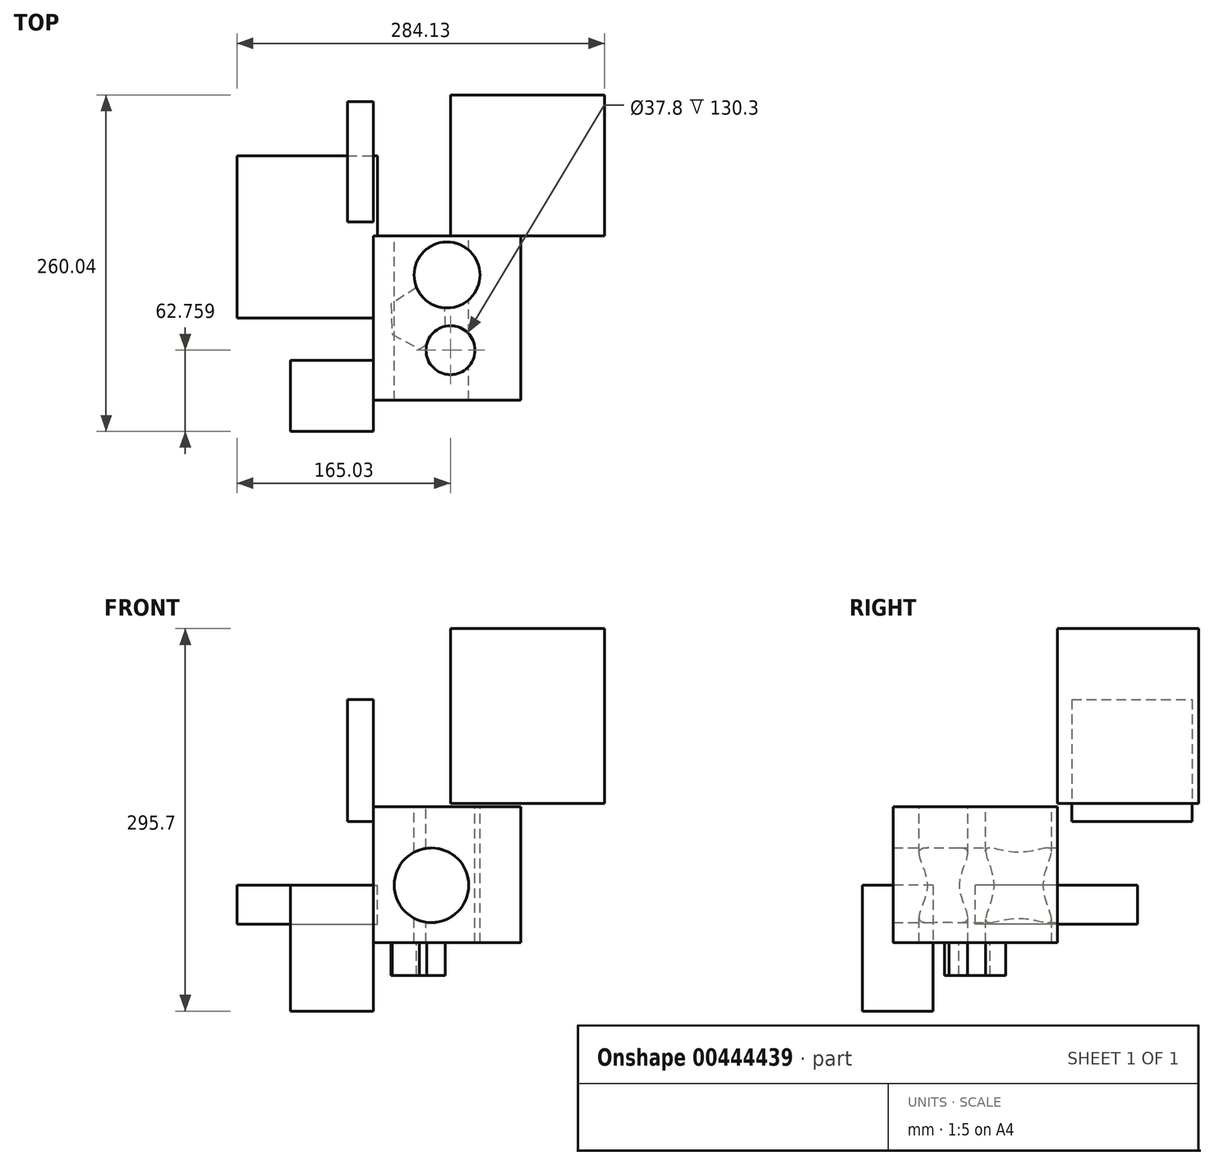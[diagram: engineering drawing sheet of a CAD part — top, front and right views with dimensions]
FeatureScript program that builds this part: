
annotation { "Feature Type Name" : "Feature", "Feature Type Description" : "" }
export const myFeature = defineFeature(function(context is Context, id is Id, definition is map)
    precondition{}
    {
        {
            var Q0;
            Q0=qCreatedBy(makeId("Front.planeOp"),FACE);
            var sketch = newSketch(context, id + "F0", { "sketchPlane" : qUnion([Q0])});
            skLineSegment(sketch, "E0.bottom", {"start": v(-59.68, 60.6) * mm, "end": v(54.4, 60.6) * mm});
            skLineSegment(sketch, "E0.top", {"start": v(-59.68, -44.3) * mm, "end": v(54.4, -44.3) * mm});
            skLineSegment(sketch, "E0.left", {"start": v(-59.68, 60.6) * mm, "end": v(-59.68, -44.3) * mm});
            skLineSegment(sketch, "E0.right", {"start": v(54.4, 60.6) * mm, "end": v(54.4, -44.3) * mm});
            skSolve(sketch);
        }
        {
            var Q0;
            Q0=makeQuery(id+"F0.imprint","IMPRINT",FACE,{"disambiguationData":[TD([[makeQuery(id+"F0.imprint","IMPRINT",EDGE,{"derivedFrom":sQuery(id+"F0.wireOp",EDGE,"E0.bottom")}),-1.0]])]});
            extrude(context, id + "F1", {"entities" : qUnion([Q0]), "endBound" : BoundingType.SYMMETRIC, "oppositeDirection" : true, "depth" : 127 * mm});
        }
        {
            var Q0;
            Q0=qCreatedBy(makeId("Front.planeOp"),FACE);
            var sketch = newSketch(context, id + "F2", { "sketchPlane" : qUnion([Q0])});
            skLineSegment(sketch, "E1", {"start": v(-104.47, 48.32) * mm, "end": v(17.34, -36.07) * mm});
            skLineSegment(sketch, "E2.0", {"start": v(-59.68, 60.6) * mm, "end": v(54.4, 60.6) * mm});
            skLineSegment(sketch, "E3.0.0", {"start": v(-59.68, 60.6) * mm, "end": v(-59.68, -44.3) * mm});
            skLineSegment(sketch, "E3.0.1", {"start": v(-59.68, -44.3) * mm, "end": v(54.4, -44.3) * mm});
            skLineSegment(sketch, "E3.0.2", {"start": v(54.4, -44.3) * mm, "end": v(54.4, 60.6) * mm});
            skLineSegment(sketch, "E3.0.3", {"start": v(54.4, 60.6) * mm, "end": v(-59.68, 60.6) * mm});
            skSolve(sketch);
        }
        {
            var Q0;
            Q0=makeQuery(id+"F1.opExtrude","CAP_FACE",FACE,{"disambiguationData":[OSD([sQuery(id+"F0.wireOp",EDGE,"E0.bottom"),sQuery(id+"F0.wireOp",EDGE,"E0.top"),sQuery(id+"F0.wireOp",EDGE,"E0.left"),sQuery(id+"F0.wireOp",EDGE,"E0.right")])],"isStart":false});
            var sketch = newSketch(context, id + "F3", { "sketchPlane" : qUnion([Q0])});
            skCircle(sketch, "E4", {"center": v(14.7, 0) * mm, "radius": 28.82 * mm});
            skSolve(sketch);
        }
        {
            var Q0;
            Q0=makeQuery(id+"F3.imprint","IMPRINT",FACE,{"disambiguationData":[TD([[makeQuery(id+"F3.imprint","IMPRINT",EDGE,{"derivedFrom":sQuery(id+"F3.wireOp",EDGE,"E4")}),1.0]])]});
            extrude(context, id + "F4", {"entities" : qUnion([Q0]), "operationType" : NewBodyOperationType.REMOVE, "oppositeDirection" : true, "depth" : 181.76 * mm});
        }
        {
            var Q0;
            Q0=makeQuery(id+"F1.opExtrude","SWEPT_FACE",FACE,{"disambiguationData":[OSD([sQuery(id+"F0.wireOp",EDGE,"E0.top")])]});
            var sketch = newSketch(context, id + "F5", { "sketchPlane" : qUnion([Q0])});
            skSolve(sketch);
        }
        {
            var Q0;
            {var subQ0=sQuery(id+"F0.wireOp",EDGE,"E0.top");Q0=makeQuery(id+"F5.imprint","IMPRINT",FACE,{"disambiguationData":[TD([[makeQuery(id+"F5.imprint","IMPRINT",EDGE,{"derivedFrom":makeQuery(id+"F1.opExtrude","CAP_EDGE",EDGE,{"disambiguationData":[OSD([subQ0])],"isStart":true})}),-1.0]])]});}
            var sketch = newSketch(context, id + "F6", { "sketchPlane" : qUnion([Q0])});
            skCircle(sketch, "E5.cCircle", {"center": v(-24.85, 0) * mm, "radius": 20.67 * mm, "construction": true});
            skLineSegment(sketch, "E5.0", {"start": v(-24.05, 23.85) * mm, "end": v(-3.8, 11.23) * mm});
            skLineSegment(sketch, "E5.1", {"start": v(-3.8, 11.23) * mm, "end": v(-4.6, -12.62) * mm});
            skLineSegment(sketch, "E5.2", {"start": v(-4.6, -12.62) * mm, "end": v(-25.65, -23.85) * mm});
            skLineSegment(sketch, "E5.3", {"start": v(-25.65, -23.85) * mm, "end": v(-45.9, -11.23) * mm});
            skLineSegment(sketch, "E5.4", {"start": v(-45.9, -11.23) * mm, "end": v(-45.1, 12.62) * mm});
            skLineSegment(sketch, "E5.5", {"start": v(-45.1, 12.62) * mm, "end": v(-24.05, 23.85) * mm});
            skPoint(sketch, "E5.0.midPoint", {"position": v(-13.93, 17.54) * mm});
            skSolve(sketch);
        }
        {
            var Q0;
            Q0=makeQuery(id+"F6.imprint","IMPRINT",FACE,{"disambiguationData":[TD([[makeQuery(id+"F6.imprint","IMPRINT",EDGE,{"derivedFrom":sQuery(id+"F6.wireOp",EDGE,"E5.0")}),-1.0]])]});
            extrude(context, id + "F7", {"entities" : qUnion([Q0]), "operationType" : NewBodyOperationType.ADD, "depth" : 25.4 * mm});
        }
        {
            var Q0;
            Q0 = qSketchRegion(id + "F2", true);
            var sketch = newSketch(context, id + "F8", { "sketchPlane" : qUnion([Q0])});
            skLineSegment(sketch, "E6.bottom", {"start": v(-165.03, -30.2) * mm, "end": v(-56.33, -30.2) * mm});
            skLineSegment(sketch, "E6.top", {"start": v(-165.03, 0) * mm, "end": v(-56.33, 0) * mm});
            skLineSegment(sketch, "E6.left", {"start": v(-165.03, -30.2) * mm, "end": v(-165.03, 0) * mm});
            skLineSegment(sketch, "E6.right", {"start": v(-56.33, -30.2) * mm, "end": v(-56.33, 0) * mm});
            skSolve(sketch);
        }
        {
            var Q0;
            Q0 = qSketchRegion(id + "F8", true);
            extrude(context, id + "F9", {"entities" : qUnion([Q0]), "operationType" : NewBodyOperationType.ADD, "oppositeDirection" : true, "depth" : 125.48 * mm});
        }
        {
            var Q0;
            Q0=makeQuery(id+"F1.opExtrude","SWEPT_FACE",FACE,{"disambiguationData":[OSD([sQuery(id+"F0.wireOp",EDGE,"E0.left")])]});
            var sketch = newSketch(context, id + "F10", { "sketchPlane" : qUnion([Q0])});
            skLineSegment(sketch, "E7", {"start": v(-116.28, 254.28) * mm, "end": v(-116.28, 223.5) * mm});
            skLineSegment(sketch, "E8", {"start": v(-116.28, 223.5) * mm, "end": v(0, 223.5) * mm});
            skLineSegment(sketch, "E9.bottom", {"start": v(-74.53, 143.6) * mm, "end": v(-167.43, 143.6) * mm});
            skLineSegment(sketch, "E9.top", {"start": v(-74.53, 49.3) * mm, "end": v(-167.43, 49.3) * mm});
            skLineSegment(sketch, "E9.left", {"start": v(-74.53, 143.6) * mm, "end": v(-74.53, 49.3) * mm});
            skLineSegment(sketch, "E9.right", {"start": v(-167.43, 143.6) * mm, "end": v(-167.43, 49.3) * mm});
            skSolve(sketch);
        }
        {
            var Q0;
            Q0 = qSketchRegion(id + "F10", true);
            extrude(context, id + "F11", {"entities" : qUnion([Q0]), "depth" : 20 * mm});
        }
        {
            var Q0;
            Q0=makeQuery(id+"F1.opExtrude","SWEPT_FACE",FACE,{"disambiguationData":[OSD([sQuery(id+"F0.wireOp",EDGE,"E0.bottom")])]});
            var sketch = newSketch(context, id + "F12", { "sketchPlane" : qUnion([Q0])});
            skCircle(sketch, "E10", {"center": v(0, -24.73) * mm, "radius": 18.9 * mm});
            skCircle(sketch, "E11", {"center": v(-2.64, 33.4) * mm, "radius": 25.5 * mm});
            skPoint(sketch, "E11.centerSnap0", {"position": v(-2.64, -63.5) * mm});
            skSolve(sketch);
        }
        {
            var Q0;
            Q0 = qSketchRegion(id + "F12", true);
            extrude(context, id + "F13", {"entities" : qUnion([Q0]), "operationType" : NewBodyOperationType.REMOVE, "oppositeDirection" : true, "depth" : 174.7 * mm});
        }
        {
            var Q0;
            Q0=makeQuery(id+"F1.opExtrude","SWEPT_FACE",FACE,{"disambiguationData":[OSD([sQuery(id+"F0.wireOp",EDGE,"E0.left")])]});
            var sketch = newSketch(context, id + "F14", { "sketchPlane" : qUnion([Q0])});
            skLineSegment(sketch, "E12.bottom", {"start": v(32.6, 0) * mm, "end": v(87.49, 0) * mm});
            skLineSegment(sketch, "E12.top", {"start": v(32.6, -97.27) * mm, "end": v(87.49, -97.27) * mm});
            skLineSegment(sketch, "E12.left", {"start": v(32.6, 0) * mm, "end": v(32.6, -97.27) * mm});
            skLineSegment(sketch, "E12.right", {"start": v(87.49, 0) * mm, "end": v(87.49, -97.27) * mm});
            skSolve(sketch);
        }
        {
            var Q0;
            Q0 = qSketchRegion(id + "F14", true);
            extrude(context, id + "F15", {"entities" : qUnion([Q0]), "operationType" : NewBodyOperationType.ADD, "depth" : 63.97 * mm});
        }
        {
            var Q0;
            Q0=makeQuery(id+"F1.opExtrude","CAP_FACE",FACE,{"disambiguationData":[OSD([sQuery(id+"F0.wireOp",EDGE,"E0.bottom"),sQuery(id+"F0.wireOp",EDGE,"E0.top"),sQuery(id+"F0.wireOp",EDGE,"E0.left"),sQuery(id+"F0.wireOp",EDGE,"E0.right")])],"isStart":false});
            var sketch = newSketch(context, id + "F16", { "sketchPlane" : qUnion([Q0])});
            skLineSegment(sketch, "E13.bottom", {"start": v(-119.1, 63.2) * mm, "end": v(0, 63.2) * mm});
            skLineSegment(sketch, "E13.top", {"start": v(-119.1, 198.43) * mm, "end": v(0, 198.43) * mm});
            skLineSegment(sketch, "E13.left", {"start": v(-119.1, 63.2) * mm, "end": v(-119.1, 198.43) * mm});
            skLineSegment(sketch, "E13.right", {"start": v(0, 63.2) * mm, "end": v(0, 198.43) * mm});
            skSolve(sketch);
        }
        {
            var Q0;
            Q0 = qSketchRegion(id + "F16", true);
            extrude(context, id + "F17", {"entities" : qUnion([Q0]), "depth" : 109.05 * mm});
        }
    });
